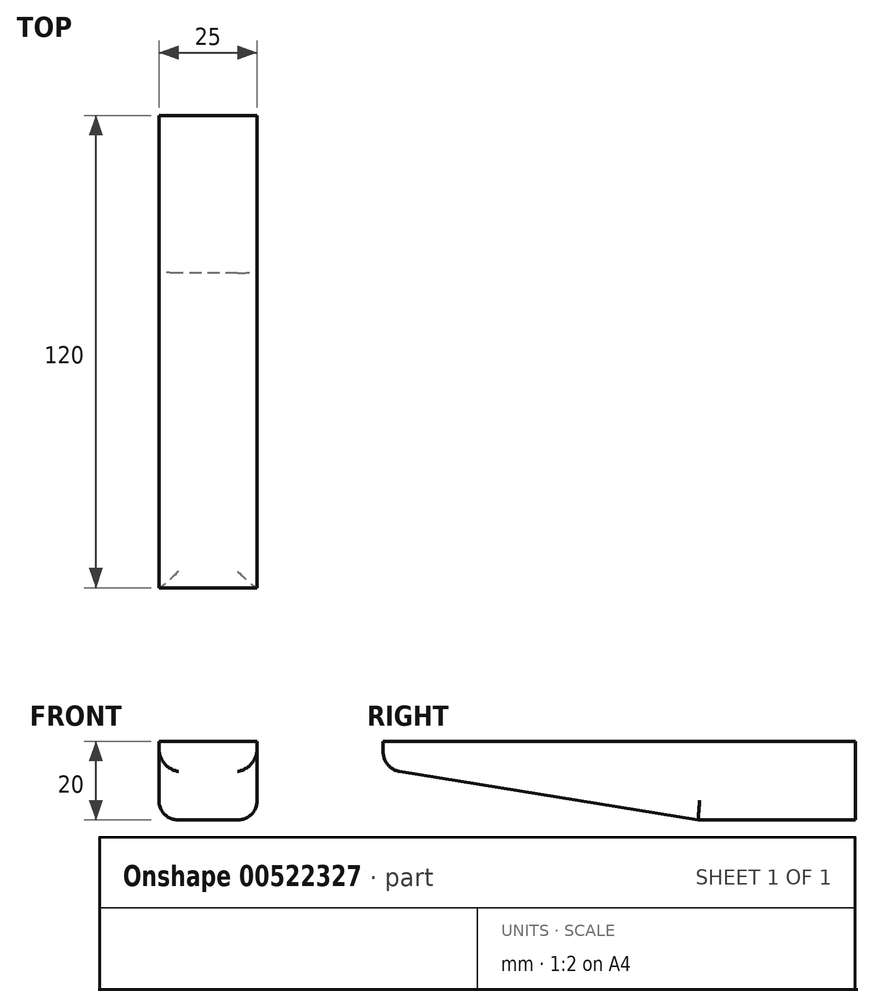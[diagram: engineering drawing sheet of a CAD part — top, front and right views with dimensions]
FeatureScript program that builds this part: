
annotation { "Feature Type Name" : "Feature", "Feature Type Description" : "" }
export const myFeature = defineFeature(function(context is Context, id is Id, definition is map)
    precondition{}
    {
        {
            var Q0;
            Q0=qCreatedBy(makeId("Right.planeOp"),FACE);
            var sketch = newSketch(context, id + "F0", { "sketchPlane" : qUnion([Q0])});
            skLineSegment(sketch, "E0", {"start": v(0, 0) * mm, "end": v(0, -20) * mm});
            skLineSegment(sketch, "E1", {"start": v(-120, -7) * mm, "end": v(-120, 0) * mm});
            skLineSegment(sketch, "E2", {"start": v(-120, 0) * mm, "end": v(0, 0) * mm});
            skLineSegment(sketch, "E3", {"start": v(0, -20) * mm, "end": v(-40, -20) * mm});
            skLineSegment(sketch, "E4", {"start": v(-40, -20) * mm, "end": v(-120, -7) * mm});
            skSolve(sketch);
        }
        {
            var Q0;
            Q0 = qSketchRegion(id + "F0", true);
            extrude(context, id + "F1", {"entities" : qUnion([Q0]), "depth" : 25 * mm, "offsetDistance" : 25 * mm});
        }
        {
            var Q0;
            Q0=makeQuery(id+"F1.opExtrude","CAP_EDGE",EDGE,{"disambiguationData":[OSD([sQuery(id+"F0.wireOp",EDGE,"E3")])],"isStart":false});
            var Q1;
            Q1=makeQuery(id+"F1.opExtrude","CAP_EDGE",EDGE,{"disambiguationData":[OSD([sQuery(id+"F0.wireOp",EDGE,"E4")])],"isStart":false});
            var Q2;
            Q2=makeQuery(id+"F1.opExtrude","SWEPT_EDGE",EDGE,{"disambiguationData":[OSD([sQuery(id+"F0.wireOp",EDGE,"E1"),sQuery(id+"F0.wireOp",EDGE,"E4")])]});
            var Q3;
            Q3=makeQuery(id+"F1.opExtrude","CAP_EDGE",EDGE,{"disambiguationData":[OSD([sQuery(id+"F0.wireOp",EDGE,"E4")])],"isStart":true});
            var Q4;
            Q4=makeQuery(id+"F1.opExtrude","CAP_EDGE",EDGE,{"disambiguationData":[OSD([sQuery(id+"F0.wireOp",EDGE,"E3")])],"isStart":true});
            fillet(context, id + "F2", {"entities" : qUnion([Q0, Q1, Q2, Q3, Q4]), "radius" : 5 * mm, "tangentPropagation" : true, "allowEdgeOverflow" : false});
        }
    });
